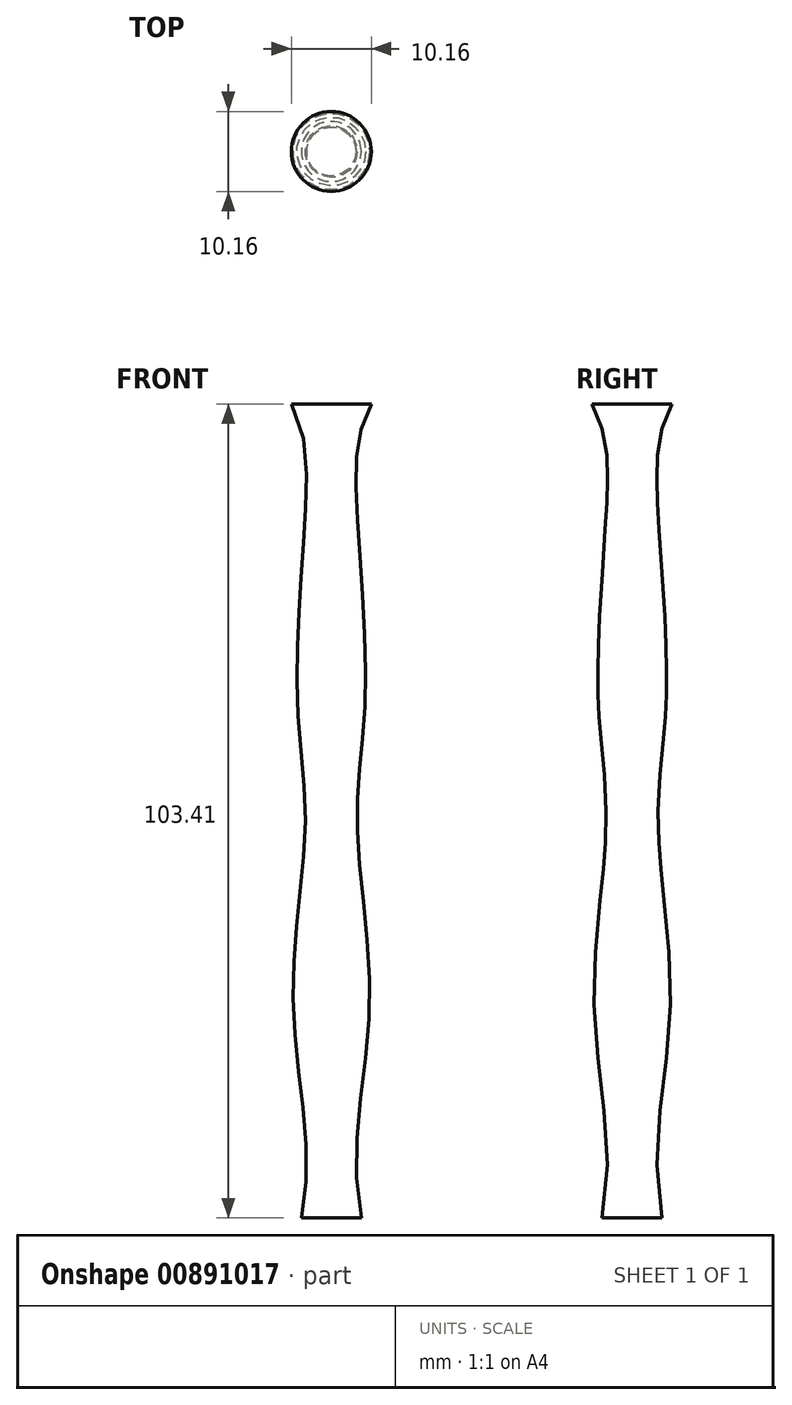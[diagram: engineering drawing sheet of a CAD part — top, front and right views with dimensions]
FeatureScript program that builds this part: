
annotation { "Feature Type Name" : "Feature", "Feature Type Description" : "" }
export const myFeature = defineFeature(function(context is Context, id is Id, definition is map)
    precondition{}
    {
        {
            var Q0;
            Q0=qCreatedBy(makeId("Front.planeOp"),FACE);
            var sketch = newSketch(context, id + "F0", { "sketchPlane" : qUnion([Q0])});
            skFitSpline(sketch, "E0", {"points": [v(-5.08, 53.52) * mm, v(-3.3, 39.6) * mm, v(-4.32, 16.2) * mm, v(-3.3, 0) * mm, v(-4.83, -23.32) * mm, v(-3.81, -49.89) * mm], "startDerivative": vector(40.04, -73.68) * mm, "endDerivative": vector(-23.65, -117.02) * mm});
            skLineSegment(sketch, "E1", {"start": v(-5.08, 53.52) * mm, "end": v(0, 53.52) * mm});
            skLineSegment(sketch, "E2", {"start": v(-3.81, -49.89) * mm, "end": v(0, -49.89) * mm});
            skLineSegment(sketch, "E3", {"start": v(0, 53.52) * mm, "end": v(0, -49.89) * mm});
            skSolve(sketch);
        }
        {
            var Q0;
            Q0=makeQuery(id+"F0.imprint","IMPRINT",FACE,{"disambiguationData":[TD([[makeQuery(id+"F0.imprint","IMPRINT",EDGE,{"derivedFrom":sQuery(id+"F0.wireOp",EDGE,"E0")}),1.0]])]});
            var Q1;
            Q1=sQuery(id+"F0.wireOp",EDGE,"E3");
            revolve(context, id + "F1", {"surfaceOperationType" : NewSurfaceOperationType.NEW, "entities" : qUnion([Q0]), "axis" : qUnion([Q1]), "revolveType" : RevolveType.FULL});
        }
    });
